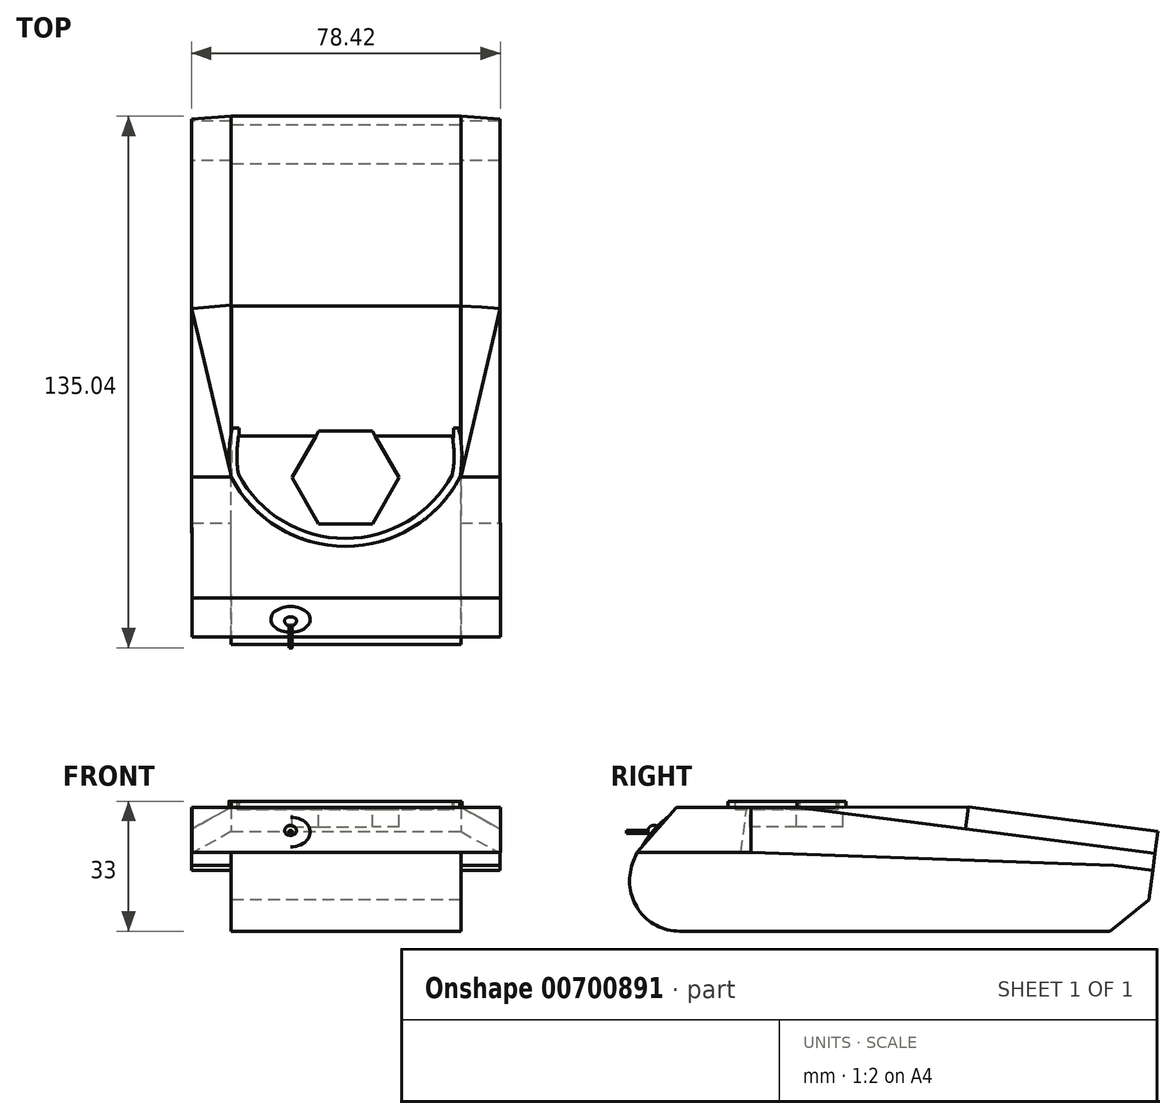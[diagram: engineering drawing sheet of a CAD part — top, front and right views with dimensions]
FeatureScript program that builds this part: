
annotation { "Feature Type Name" : "Feature", "Feature Type Description" : "" }
export const myFeature = defineFeature(function(context is Context, id is Id, definition is map)
    precondition{}
    {
        {
            var Q0;
            Q0=qCreatedBy(makeId("Top.planeOp"),FACE);
            var sketch = newSketch(context, id + "F0", { "sketchPlane" : qUnion([Q0])});
            skLineSegment(sketch, "E0.bottom", {"start": v(33.12, -52.33) * mm, "end": v(-25.22, -52.33) * mm});
            skLineSegment(sketch, "E0.top", {"start": v(33.12, 75.36) * mm, "end": v(-25.22, 75.36) * mm});
            skLineSegment(sketch, "E0.left", {"start": v(33.12, -52.33) * mm, "end": v(33.12, 75.36) * mm});
            skLineSegment(sketch, "E0.right", {"start": v(-25.22, -52.33) * mm, "end": v(-25.22, 75.36) * mm});
            skSolve(sketch);
        }
        {
            var Q0;
            Q0 = qSketchRegion(id + "F0", true);
            extrude(context, id + "F1", {"entities" : qUnion([Q0]), "depth" : 20 * mm, "offsetDistance" : 25 * mm});
        }
        {
            var Q0;
            Q0=makeQuery(id+"F1.opExtrude","CAP_FACE",FACE,{"disambiguationData":[OSD([sQuery(id+"F0.wireOp",EDGE,"E0.bottom"),sQuery(id+"F0.wireOp",EDGE,"E0.top"),sQuery(id+"F0.wireOp",EDGE,"E0.left"),sQuery(id+"F0.wireOp",EDGE,"E0.right")])],"isStart":false});
            var sketch = newSketch(context, id + "F2", { "sketchPlane" : qUnion([Q0])});
            skLineSegment(sketch, "E1", {"start": v(33.12, -52.33) * mm, "end": v(43.12, -52.33) * mm});
            skLineSegment(sketch, "E2", {"start": v(43.12, -52.33) * mm, "end": v(-25.22, -52.33) * mm});
            skLineSegment(sketch, "E3", {"start": v(-25.22, -52.33) * mm, "end": v(-35.22, -52.33) * mm});
            skLineSegment(sketch, "E4.bottom", {"start": v(43.12, -52.33) * mm, "end": v(-35.22, -52.33) * mm});
            skLineSegment(sketch, "E4.top", {"start": v(43.12, 75.36) * mm, "end": v(-35.22, 75.36) * mm});
            skLineSegment(sketch, "E4.left", {"start": v(43.12, -52.33) * mm, "end": v(43.12, 75.36) * mm});
            skLineSegment(sketch, "E4.right", {"start": v(-35.22, -52.33) * mm, "end": v(-35.22, 75.36) * mm});
            skLineSegment(sketch, "E5", {"start": v(43.12, -52.33) * mm, "end": v(43.12, -44.83) * mm});
            skLineSegment(sketch, "E6", {"start": v(43.12, -34.83) * mm, "end": v(-35.22, -34.83) * mm});
            skLineSegment(sketch, "E7", {"start": v(-35.22, -34.83) * mm, "end": v(-35.22, -44.83) * mm});
            skLineSegment(sketch, "E8", {"start": v(33.12, -34.83) * mm, "end": v(-25.22, -34.83) * mm});
            skLineSegment(sketch, "E9", {"start": v(43.12, -44.83) * mm, "end": v(33.12, -44.83) * mm});
            skLineSegment(sketch, "E10", {"start": v(33.12, -44.83) * mm, "end": v(-25.22, -44.83) * mm});
            skLineSegment(sketch, "E11", {"start": v(-25.22, -44.83) * mm, "end": v(-35.22, -44.83) * mm});
            skLineSegment(sketch, "E12", {"start": v(0, -34.83) * mm, "end": v(0, -52.33) * mm});
            skLineSegment(sketch, "E13", {"start": v(0, -52.33) * mm, "end": v(0, -34.83) * mm});
            skLineSegment(sketch, "E14", {"start": v(0, -34.83) * mm, "end": v(0, 75.36) * mm});
            skLineSegment(sketch, "E15.top", {"start": v(33.12, -15.83) * mm, "end": v(-25.22, -15.83) * mm});
            skLineSegment(sketch, "E15.left", {"start": v(33.12, -34.83) * mm, "end": v(33.12, -15.83) * mm});
            skLineSegment(sketch, "E15.right", {"start": v(-25.22, -34.83) * mm, "end": v(-25.22, -15.83) * mm});
            skLineSegment(sketch, "E16", {"start": v(33.12, -15.83) * mm, "end": v(43.12, -15.83) * mm});
            skLineSegment(sketch, "E17", {"start": v(43.12, -15.83) * mm, "end": v(-25.22, -15.83) * mm});
            skLineSegment(sketch, "E18", {"start": v(-25.22, -15.83) * mm, "end": v(-35.22, -15.83) * mm});
            skSolve(sketch);
        }
        {
            var Q0;
            {var subQ0=sQuery(id+"F2.wireOp",EDGE,"E15.left");Q0=makeQuery(id+"F2.imprint","IMPRINT",FACE,{"disambiguationData":[TD([[makeQuery(id+"F2.imprint","IMPRINT",EDGE,{"derivedFrom":subQ0}),1.0]])]});}
            var Q1;
            {var subQ3=sQuery(id+"F2.wireOp",EDGE,"E15.right");Q1=makeQuery(id+"F2.imprint","IMPRINT",FACE,{"disambiguationData":[TD([[makeQuery(id+"F2.imprint","IMPRINT",EDGE,{"derivedFrom":subQ3}),-1.0]])]});}
            extrude(context, id + "F3", {"entities" : qUnion([Q0, Q1]), "operationType" : NewBodyOperationType.ADD, "depth" : 11.5 * mm, "offsetDistance" : 25 * mm});
        }
        {
            var Q0;
            {var subQ0=sQuery(id+"F2.wireOp",EDGE,"E12");var subQ5=sQuery(id+"F2.wireOp",EDGE,"E10");var subQ7=makeQuery(id+"F2.imprint","INTERSECT",VERTEX,{"derivedFrom":[subQ5,subQ0]});Q0=makeQuery(id+"F2.imprint","IMPRINT",FACE,{"disambiguationData":[TD([[makeQuery(id+"F2.imprint","IMPRINT",EDGE,{"disambiguationData":[TD([[subQ7,-1.0]])],"derivedFrom":subQ5}),-1.0]])]});}
            var Q1;
            {var subQ3=sQuery(id+"F2.wireOp",EDGE,"E12");var subQ5=sQuery(id+"F2.wireOp",EDGE,"E10");var subQ7=makeQuery(id+"F2.imprint","INTERSECT",VERTEX,{"derivedFrom":[subQ5,subQ3]});Q1=makeQuery(id+"F2.imprint","IMPRINT",FACE,{"disambiguationData":[TD([[makeQuery(id+"F2.imprint","IMPRINT",EDGE,{"disambiguationData":[TD([[subQ7,1.0]])],"derivedFrom":subQ5}),-1.0]])]});}
            var Q2;
            {var subQ0=sQuery(id+"F2.wireOp",EDGE,"E9");Q2=makeQuery(id+"F2.imprint","IMPRINT",FACE,{"disambiguationData":[TD([[makeQuery(id+"F2.imprint","IMPRINT",EDGE,{"derivedFrom":subQ0}),-1.0]])]});}
            var Q3;
            {var subQ0=sQuery(id+"F2.wireOp",EDGE,"E11");Q3=makeQuery(id+"F2.imprint","IMPRINT",FACE,{"disambiguationData":[TD([[makeQuery(id+"F2.imprint","IMPRINT",EDGE,{"derivedFrom":subQ0}),-1.0]])]});}
            var Q4;
            {var subQ4=sQuery(id+"F2.wireOp",EDGE,"E15.right");Q4=makeQuery(id+"F2.imprint","IMPRINT",FACE,{"disambiguationData":[TD([[makeQuery(id+"F2.imprint","IMPRINT",EDGE,{"derivedFrom":subQ4}),1.0]])]});}
            var Q5;
            {var subQ4=sQuery(id+"F2.wireOp",EDGE,"E15.left");Q5=makeQuery(id+"F2.imprint","IMPRINT",FACE,{"disambiguationData":[TD([[makeQuery(id+"F2.imprint","IMPRINT",EDGE,{"derivedFrom":subQ4}),-1.0]])]});}
            extrude(context, id + "F4", {"entities" : qUnion([Q0, Q1, Q2, Q3, Q4, Q5]), "operationType" : NewBodyOperationType.ADD, "depth" : 11.5 * mm, "offsetDistance" : 25 * mm});
        }
        {
            var Q0;
            Q0=makeQuery(id+"F4.opExtrude","CAP_EDGE",EDGE,{"disambiguationData":[OSD([sQuery(id+"F2.wireOp",EDGE,"E9"),sQuery(id+"F2.wireOp",EDGE,"E10"),sQuery(id+"F2.wireOp",EDGE,"E11")])],"isStart":false});
            chamfer(context, id + "F5", {"entities" : qUnion([Q0]), "chamferType" : ChamferType.TWO_OFFSETS, "width1" : 11.5 * mm, "oppositeDirection" : false, "width2" : 10 * mm, "tangentPropagation" : true});
        }
        {
            var Q0;
            Q0=makeQuery(id+"F4.opExtrude","SWEPT_FACE",FACE,{"disambiguationData":[OSD([sQuery(id+"F2.wireOp",EDGE,"E4.right")])]});
            var sketch = newSketch(context, id + "F6", { "sketchPlane" : qUnion([Q0])});
            skLineSegment(sketch, "E19", {"start": v(15.83, 31.5) * mm, "end": v(-75.36, 20) * mm});
            skSolve(sketch);
        }
        {
            var Q0;
            {var subQ0=sQuery(id+"F2.wireOp",EDGE,"E15.right");var subQ1=sQuery(id+"F2.wireOp",EDGE,"E15.left");var subQ2=sQuery(id+"F2.wireOp",EDGE,"E6");Q0=makeQuery(id+"F4.boolean.opBoolean","MERGE",FACE,{"derivedFrom":[makeQuery(id+"F3.opExtrude","CAP_FACE",FACE,{"disambiguationData":[OSD([subQ2,sQuery(id+"F2.wireOp",EDGE,"E15.top"),subQ1,subQ0])],"isStart":false}),makeQuery(id+"F4.opExtrude","CAP_FACE",FACE,{"disambiguationData":[OSD([sQuery(id+"F2.wireOp",EDGE,"E4.left"),sQuery(id+"F2.wireOp",EDGE,"E4.right"),subQ2,sQuery(id+"F2.wireOp",EDGE,"E9"),sQuery(id+"F2.wireOp",EDGE,"E10"),sQuery(id+"F2.wireOp",EDGE,"E11"),subQ1,subQ0,sQuery(id+"F2.wireOp",EDGE,"E16"),sQuery(id+"F2.wireOp",EDGE,"E18")])],"isStart":false})]});}
            var sketch = newSketch(context, id + "F7", { "sketchPlane" : qUnion([Q0])});
            skLineSegment(sketch, "E20.bottom", {"start": v(-35.22, -15.83) * mm, "end": v(43.12, -15.83) * mm});
            skLineSegment(sketch, "E20.top", {"start": v(-35.22, 75) * mm, "end": v(43.12, 75) * mm});
            skLineSegment(sketch, "E20.left", {"start": v(-35.22, -15.83) * mm, "end": v(-35.22, 75) * mm});
            skLineSegment(sketch, "E20.right", {"start": v(43.12, -15.83) * mm, "end": v(43.12, 75) * mm});
            skSolve(sketch);
        }
        {
            var Q0;
            Q0=sQuery(id+"F7.wireOp",EDGE,"E20.bottom");
            cPlane(context, id + "F8", {"entities" : qUnion([Q0]), "cplaneType" : CPlaneType.LINE_ANGLE, "offset" : 11.5 * mm, "angle" : 97.33 * degree, "oppositeDirection" : true, "width" : 150 * mm, "height" : 150 * mm});
        }
        {
            var Q0;
            Q0=qCreatedBy(id+"F8.planeOp",FACE);
            var sketch = newSketch(context, id + "F9", { "sketchPlane" : qUnion([Q0])});
            skLineSegment(sketch, "E21.bottom", {"start": v(-35.3, 20.78) * mm, "end": v(43.04, 20.78) * mm});
            skLineSegment(sketch, "E21.top", {"start": v(-35.3, -73.57) * mm, "end": v(43.04, -73.57) * mm});
            skLineSegment(sketch, "E21.left", {"start": v(-35.3, 20.78) * mm, "end": v(-35.3, -73.57) * mm});
            skLineSegment(sketch, "E21.right", {"start": v(43.04, 20.78) * mm, "end": v(43.04, -73.57) * mm});
            skSolve(sketch);
        }
        {
            var Q0;
            Q0 = qSketchRegion(id + "F9", true);
            extrude(context, id + "F10", {"entities" : qUnion([Q0]), "operationType" : NewBodyOperationType.ADD, "depth" : 11.7 * mm, "offsetDistance" : 25 * mm});
        }
        {
            var Q0;
            {var subQ0=sQuery(id+"F9.wireOp",EDGE,"E21.top");Q0=makeQuery(id+"F10.boolean.opBoolean","SPLIT",EDGE,{"disambiguationData":[TD([makeQuery(id+"F1.opExtrude","SWEPT_FACE",FACE,{"disambiguationData":[OSD([sQuery(id+"F0.wireOp",EDGE,"E0.left")])]})])],"derivedFrom":makeQuery(id+"F10.opExtrude","CAP_EDGE",EDGE,{"disambiguationData":[OSD([subQ0])],"isStart":false})});}
            var Q1;
            {var subQ1=sQuery(id+"F9.wireOp",EDGE,"E21.top");Q1=makeQuery(id+"F10.boolean.opBoolean","SPLIT",EDGE,{"disambiguationData":[TD([makeQuery(id+"F1.opExtrude","SWEPT_FACE",FACE,{"disambiguationData":[OSD([sQuery(id+"F0.wireOp",EDGE,"E0.right")])]})])],"derivedFrom":makeQuery(id+"F10.opExtrude","CAP_EDGE",EDGE,{"disambiguationData":[OSD([subQ1])],"isStart":false})});}
            chamfer(context, id + "F11", {"entities" : qUnion([Q0, Q1]), "chamferType" : ChamferType.TWO_OFFSETS, "width1" : 8.75 * mm, "oppositeDirection" : true, "width2" : 95 * mm, "tangentPropagation" : true});
        }
        {
            var Q0;
            Q0=makeQuery(id+"F10.opExtrude","CAP_FACE",FACE,{"disambiguationData":[OSD([sQuery(id+"F9.wireOp",EDGE,"E21.bottom"),sQuery(id+"F9.wireOp",EDGE,"E21.top"),sQuery(id+"F9.wireOp",EDGE,"E21.left"),sQuery(id+"F9.wireOp",EDGE,"E21.right")])],"isStart":true});
            extrude(context, id + "F12", {"entities" : qUnion([Q0]), "operationType" : NewBodyOperationType.ADD, "depth" : 1.5 * mm, "offsetDistance" : 25 * mm});
        }
        {
            var Q0;
            {var subQ0=sQuery(id+"F9.wireOp",EDGE,"E21.top");Q0=makeQuery(id+"F12.boolean.opBoolean","MERGE",FACE,{"derivedFrom":[makeQuery(id+"F10.opExtrude","SWEPT_FACE",FACE,{"disambiguationData":[OSD([subQ0])]}),makeQuery(id+"F12.opExtrude","SWEPT_FACE",FACE,{"disambiguationData":[OSD([subQ0])]})]});}
            var sketch = newSketch(context, id + "F13", { "sketchPlane" : qUnion([Q0])});
            skLineSegment(sketch, "E22.bottom", {"start": v(-43.04, 26.27) * mm, "end": v(35.3, 26.27) * mm});
            skLineSegment(sketch, "E22.top", {"start": v(-43.04, 30.72) * mm, "end": v(35.3, 30.72) * mm});
            skLineSegment(sketch, "E22.left", {"start": v(-43.04, 26.27) * mm, "end": v(-43.04, 30.72) * mm});
            skLineSegment(sketch, "E22.right", {"start": v(35.3, 26.27) * mm, "end": v(35.3, 30.72) * mm});
            skLineSegment(sketch, "E23", {"start": v(-33.12, 26.27) * mm, "end": v(25.22, 26.27) * mm});
            skLineSegment(sketch, "E24", {"start": v(25.22, 26.27) * mm, "end": v(-3.95, 26.27) * mm});
            skLineSegment(sketch, "E25", {"start": v(10.63, 26.27) * mm, "end": v(-3.95, 26.27) * mm});
            skLineSegment(sketch, "E26", {"start": v(-3.95, 26.27) * mm, "end": v(-33.12, 26.27) * mm});
            skLineSegment(sketch, "E27", {"start": v(-18.54, 26.27) * mm, "end": v(-3.95, 26.27) * mm});
            skLineSegment(sketch, "E28.bottom", {"start": v(-18.54, 26.27) * mm, "end": v(10.63, 26.27) * mm});
            skLineSegment(sketch, "E28.top", {"start": v(-18.54, 36.28) * mm, "end": v(10.63, 36.28) * mm});
            skLineSegment(sketch, "E28.left", {"start": v(-18.54, 26.27) * mm, "end": v(-18.54, 36.28) * mm});
            skLineSegment(sketch, "E28.right", {"start": v(10.63, 26.27) * mm, "end": v(10.63, 36.28) * mm});
            skLineSegment(sketch, "E29.bottom", {"start": v(25.22, 26.27) * mm, "end": v(10.63, 26.27) * mm});
            skLineSegment(sketch, "E29.top", {"start": v(25.22, 36.28) * mm, "end": v(10.63, 36.28) * mm});
            skLineSegment(sketch, "E29.left", {"start": v(25.22, 26.27) * mm, "end": v(25.22, 36.28) * mm});
            skLineSegment(sketch, "E30.bottom", {"start": v(-18.54, 26.27) * mm, "end": v(-33.12, 26.27) * mm});
            skLineSegment(sketch, "E30.top", {"start": v(-18.54, 36.28) * mm, "end": v(-33.12, 36.28) * mm});
            skLineSegment(sketch, "E30.right", {"start": v(-33.12, 26.27) * mm, "end": v(-33.12, 36.28) * mm});
            skLineSegment(sketch, "E31", {"start": v(25.22, 36.28) * mm, "end": v(35.3, 30.72) * mm});
            skLineSegment(sketch, "E32", {"start": v(-33.12, 36.28) * mm, "end": v(-43.04, 30.72) * mm});
            skSolve(sketch);
        }
        {
            var Q0;
            Q0 = qSketchRegion(id + "F13", true);
            extrude(context, id + "F14", {"entities" : qUnion([Q0]), "operationType" : NewBodyOperationType.ADD, "oppositeDirection" : true, "depth" : 38.55 * mm, "offsetDistance" : 25 * mm});
        }
        {
            var Q0;
            Q0=makeQuery(id+"F7.imprint","IMPRINT",FACE,{"disambiguationData":[TD([[makeQuery(id+"F7.imprint","IMPRINT",EDGE,{"derivedFrom":sQuery(id+"F7.wireOp",EDGE,"E20.bottom")}),-1.0]])]});
            var sketch = newSketch(context, id + "F15", { "sketchPlane" : qUnion([Q0])});
            skLineSegment(sketch, "E33.bottom", {"start": v(-25.2, 39.38) * mm, "end": v(33.1, 39.38) * mm});
            skLineSegment(sketch, "E33.top", {"start": v(-25.2, -14.15) * mm, "end": v(33.1, -14.15) * mm});
            skLineSegment(sketch, "E33.left", {"start": v(-25.2, 39.38) * mm, "end": v(-25.2, -14.15) * mm});
            skLineSegment(sketch, "E33.right", {"start": v(33.1, 39.38) * mm, "end": v(33.1, -14.15) * mm});
            skSolve(sketch);
        }
        {
            var Q0;
            Q0 = qSketchRegion(id + "F15", true);
            extrude(context, id + "F16", {"entities" : qUnion([Q0]), "operationType" : NewBodyOperationType.ADD, "oppositeDirection" : true, "depth" : 11.5 * mm, "offsetDistance" : 25 * mm});
        }
        {
            var Q0;
            Q0=makeQuery(id+"F14.opExtrude","CAP_VERTEX",VERTEX,{"disambiguationData":[OSD([sQuery(id+"F13.wireOp",EDGE,"E22.top"),sQuery(id+"F13.wireOp",EDGE,"E22.right"),sQuery(id+"F13.wireOp",EDGE,"E31")])],"isStart":false});
            var Q1;
            {var subQ0=sQuery(id+"F15.wireOp",EDGE,"E33.left");Q1=makeQuery(id+"F16.boolean.opBoolean","INTERSECT",VERTEX,{"derivedFrom":[makeQuery(id+"F12.opExtrude","CAP_FACE",FACE,{"disambiguationData":[OSD([sQuery(id+"F9.wireOp",EDGE,"E21.bottom"),sQuery(id+"F9.wireOp",EDGE,"E21.top"),sQuery(id+"F9.wireOp",EDGE,"E21.left"),sQuery(id+"F9.wireOp",EDGE,"E21.right")])],"isStart":false}),makeQuery(id+"F16.opExtrude","CAP_FACE",FACE,{"disambiguationData":[OSD([sQuery(id+"F15.wireOp",EDGE,"E33.bottom"),sQuery(id+"F15.wireOp",EDGE,"E33.top"),subQ0,sQuery(id+"F15.wireOp",EDGE,"E33.right")])],"isStart":true}),makeQuery(id+"F16.opExtrude","SWEPT_FACE",FACE,{"disambiguationData":[OSD([subQ0])]})]});}
            var Q2;
            Q2=makeQuery(id+"F14.opExtrude","CAP_VERTEX",VERTEX,{"disambiguationData":[OSD([sQuery(id+"F13.wireOp",EDGE,"E29.top"),sQuery(id+"F13.wireOp",EDGE,"E29.left"),sQuery(id+"F13.wireOp",EDGE,"E31")])],"isStart":false});
            cPlane(context, id + "F17", {"entities" : qUnion([Q0, Q1, Q2]), "cplaneType" : CPlaneType.THREE_POINT, "offset" : 25 * mm, "width" : 150 * mm, "height" : 150 * mm});
        }
        {
            var Q0;
            Q0=qCreatedBy(id+"F17.planeOp",FACE);
            var sketch = newSketch(context, id + "F18", { "sketchPlane" : qUnion([Q0])});
            skLineSegment(sketch, "E34", {"start": v(-7.04, -39.51) * mm, "end": v(-7.04, 4.07) * mm});
            skLineSegment(sketch, "E35", {"start": v(-7.04, 4.07) * mm, "end": v(-18.5, -38.64) * mm});
            skLineSegment(sketch, "E36", {"start": v(-18.5, -38.64) * mm, "end": v(-7.04, -39.51) * mm});
            skSolve(sketch);
        }
        {
            var Q0;
            Q0 = qSketchRegion(id + "F18", true);
            extrude(context, id + "F19", {"entities" : qUnion([Q0]), "operationType" : NewBodyOperationType.ADD, "depth" : 5.4 * mm, "offsetDistance" : 25 * mm});
        }
        {
            var Q0;
            {var subQ0=sQuery(id+"F15.wireOp",EDGE,"E33.right");Q0=makeQuery(id+"F16.boolean.opBoolean","INTERSECT",VERTEX,{"derivedFrom":[makeQuery(id+"F12.opExtrude","CAP_FACE",FACE,{"disambiguationData":[OSD([sQuery(id+"F9.wireOp",EDGE,"E21.bottom"),sQuery(id+"F9.wireOp",EDGE,"E21.top"),sQuery(id+"F9.wireOp",EDGE,"E21.left"),sQuery(id+"F9.wireOp",EDGE,"E21.right")])],"isStart":false}),makeQuery(id+"F16.opExtrude","CAP_FACE",FACE,{"disambiguationData":[OSD([sQuery(id+"F15.wireOp",EDGE,"E33.bottom"),sQuery(id+"F15.wireOp",EDGE,"E33.top"),sQuery(id+"F15.wireOp",EDGE,"E33.left"),subQ0])],"isStart":true}),makeQuery(id+"F16.opExtrude","SWEPT_FACE",FACE,{"disambiguationData":[OSD([subQ0])]})]});}
            var Q1;
            Q1=makeQuery(id+"F14.opExtrude","CAP_VERTEX",VERTEX,{"disambiguationData":[OSD([sQuery(id+"F13.wireOp",EDGE,"E22.top"),sQuery(id+"F13.wireOp",EDGE,"E22.left"),sQuery(id+"F13.wireOp",EDGE,"E32")])],"isStart":false});
            var Q2;
            Q2=makeQuery(id+"F14.opExtrude","CAP_VERTEX",VERTEX,{"disambiguationData":[OSD([sQuery(id+"F13.wireOp",EDGE,"E30.top"),sQuery(id+"F13.wireOp",EDGE,"E30.right"),sQuery(id+"F13.wireOp",EDGE,"E32")])],"isStart":false});
            cPlane(context, id + "F20", {"entities" : qUnion([Q0, Q1, Q2]), "cplaneType" : CPlaneType.THREE_POINT, "offset" : 25 * mm, "width" : 150 * mm, "height" : 150 * mm});
        }
        {
            var Q0;
            Q0=qCreatedBy(id+"F20.planeOp",FACE);
            var sketch = newSketch(context, id + "F21", { "sketchPlane" : qUnion([Q0])});
            skLineSegment(sketch, "E37", {"start": v(13.61, 4.04) * mm, "end": v(13.61, -39.38) * mm});
            skLineSegment(sketch, "E38", {"start": v(13.61, -39.38) * mm, "end": v(25, -38.67) * mm});
            skLineSegment(sketch, "E39", {"start": v(25, -38.67) * mm, "end": v(13.61, 4.04) * mm});
            skSolve(sketch);
        }
        {
            var Q0;
            Q0 = qSketchRegion(id + "F21", true);
            extrude(context, id + "F22", {"entities" : qUnion([Q0]), "operationType" : NewBodyOperationType.ADD, "depth" : 6.9 * mm, "offsetDistance" : 25 * mm});
        }
        {
            var Q0;
            {var subQ0=sQuery(id+"F9.wireOp",EDGE,"E21.left");Q0=makeQuery(id+"F12.boolean.opBoolean","MERGE",FACE,{"derivedFrom":[makeQuery(id+"F10.opExtrude","SWEPT_FACE",FACE,{"disambiguationData":[OSD([subQ0])]}),makeQuery(id+"F12.opExtrude","SWEPT_FACE",FACE,{"disambiguationData":[OSD([subQ0])]})]});}
            var sketch = newSketch(context, id + "F23", { "sketchPlane" : qUnion([Q0])});
            skLineSegment(sketch, "E40", {"start": v(16.9, 31.5) * mm, "end": v(4.08, 31.5) * mm});
            skLineSegment(sketch, "E41", {"start": v(4.08, 31.5) * mm, "end": v(16.69, 33.12) * mm});
            skLineSegment(sketch, "E42", {"start": v(16.69, 33.12) * mm, "end": v(16.9, 31.5) * mm});
            skSolve(sketch);
        }
        {
            var Q0;
            Q0 = qSketchRegion(id + "F23", true);
            extrude(context, id + "F24", {"entities" : qUnion([Q0]), "operationType" : NewBodyOperationType.REMOVE, "oppositeDirection" : true, "depth" : 83 * mm, "offsetDistance" : 25 * mm});
        }
        {
            var Q0;
            Q0=makeQuery(id+"F7.imprint","IMPRINT",FACE,{"disambiguationData":[TD([[makeQuery(id+"F7.imprint","IMPRINT",EDGE,{"derivedFrom":sQuery(id+"F7.wireOp",EDGE,"E20.bottom")}),-1.0]])]});
            var sketch = newSketch(context, id + "F25", { "sketchPlane" : qUnion([Q0])});
            skArc(sketch, "E43", {"start": v(-25.31, -4.11) * mm, "mid": v(3.75, -21.74) * mm, "end": v(32.86, -4.19) * mm});
            skArc(sketch, "E44", {"start": v(32.86, -4.19) * mm, "mid": v(33.36, 2.08) * mm, "end": v(32.52, 8.32) * mm});
            skLineSegment(sketch, "E45", {"start": v(32.52, 8.32) * mm, "end": v(-24.96, 8.32) * mm});
            skArc(sketch, "E46.trimOffspring", {"start": v(-24.96, 8.32) * mm, "mid": v(-25.8, 2.12) * mm, "end": v(-25.31, -4.11) * mm});
            skSolve(sketch);
        }
        {
            var Q0;
            {var subQ1=sQuery(id+"F0.wireOp",EDGE,"E0.right");var subQ3=sQuery(id+"F0.wireOp",EDGE,"E0.bottom");var subQ4=sQuery(id+"F2.wireOp",EDGE,"E15.right");Q0=makeQuery(id+"F10.boolean.opBoolean","SPLIT",FACE,{"disambiguationData":[TD([makeQuery(id+"F1.opExtrude","SWEPT_FACE",FACE,{"disambiguationData":[OSD([subQ3])]})])],"derivedFrom":makeQuery(id+"F3.boolean.opBoolean","MERGE",FACE,{"derivedFrom":[makeQuery(id+"F1.opExtrude","SWEPT_FACE",FACE,{"disambiguationData":[OSD([subQ1])]}),makeQuery(id+"F3.opExtrude","SWEPT_FACE",FACE,{"disambiguationData":[OSD([subQ4])]})]})});}
            var sketch = newSketch(context, id + "F26", { "sketchPlane" : qUnion([Q0])});
            skLineSegment(sketch, "E47", {"start": v(44.83, 20) * mm, "end": v(52.33, 0) * mm});
            skLineSegment(sketch, "E48", {"start": v(52.33, 0) * mm, "end": v(52.33, 20) * mm});
            skLineSegment(sketch, "E49", {"start": v(44.83, 20) * mm, "end": v(52.33, 20) * mm});
            skSolve(sketch);
        }
        {
            var Q0;
            Q0 = qSketchRegion(id + "F26", true);
            extrude(context, id + "F27", {"entities" : qUnion([Q0]), "operationType" : NewBodyOperationType.REMOVE, "oppositeDirection" : true, "depth" : 58.7 * mm, "offsetDistance" : 25 * mm});
        }
        {
            var Q0;
            Q0=makeQuery(id+"F27.boolean.opBoolean","MERGE",EDGE,{"derivedFrom":[makeQuery(id+"F1.opExtrude","CAP_EDGE",EDGE,{"disambiguationData":[OSD([sQuery(id+"F0.wireOp",EDGE,"E0.bottom")])],"isStart":true}),makeQuery(id+"F27.opExtrude","SWEPT_EDGE",EDGE,{"disambiguationData":[OSD([sQuery(id+"F0.wireOp",EDGE,"E0.right"),sQuery(id+"F26.wireOp",EDGE,"E47"),sQuery(id+"F26.wireOp",EDGE,"E48")])]})]});
            fillet(context, id + "F28", {"entities" : qUnion([Q0]), "radius" : 12.7 * mm, "tangentPropagation" : true, "allowEdgeOverflow" : false});
        }
        {
            var Q0;
            Q0=makeQuery(id+"F5.opChamfer","BLEND_FACE",FACE,{"disambiguationData":[OSD([sQuery(id+"F2.wireOp",EDGE,"E9"),sQuery(id+"F2.wireOp",EDGE,"E10"),sQuery(id+"F2.wireOp",EDGE,"E11")])]});
            var sketch = newSketch(context, id + "F29", { "sketchPlane" : qUnion([Q0])});
            skCircle(sketch, "E50", {"center": v(-10.18, -7.44) * mm, "radius": 5 * mm});
            skSolve(sketch);
        }
        {
            var Q0;
            Q0 = qSketchRegion(id + "F29", true);
            extrude(context, id + "F30", {"entities" : qUnion([Q0]), "operationType" : NewBodyOperationType.ADD, "depth" : 0.5 * mm, "offsetDistance" : 25 * mm});
        }
        {
            var Q0;
            Q0=makeQuery(id+"F30.opExtrude","CAP_EDGE",EDGE,{"disambiguationData":[OSD([sQuery(id+"F29.wireOp",EDGE,"E50")])],"isStart":false});
            fillet(context, id + "F31", {"entities" : qUnion([Q0]), "radius" : 24.87 * mm, "tangentPropagation" : true, "allowEdgeOverflow" : false});
        }
        {
            var Q0;
            Q0=makeQuery(id+"F5.opChamfer","BLEND_FACE",FACE,{"disambiguationData":[OSD([sQuery(id+"F2.wireOp",EDGE,"E9"),sQuery(id+"F2.wireOp",EDGE,"E10"),sQuery(id+"F2.wireOp",EDGE,"E11")])]});
            var sketch = newSketch(context, id + "F32", { "sketchPlane" : qUnion([Q0])});
            skCircle(sketch, "E51", {"center": v(-10.18, -7.44) * mm, "radius": 1.52 * mm});
            skSolve(sketch);
        }
        {
            var Q0;
            Q0 = qSketchRegion(id + "F32", true);
            extrude(context, id + "F33", {"entities" : qUnion([Q0]), "operationType" : NewBodyOperationType.ADD, "depth" : 1.8 * mm, "offsetDistance" : 25 * mm});
        }
        {
            var Q0;
            Q0=makeQuery(id+"F33.opExtrude","CAP_FACE",FACE,{"disambiguationData":[OSD([sQuery(id+"F32.wireOp",EDGE,"E51")])],"isStart":false});
            fillet(context, id + "F34", {"entities" : qUnion([Q0]), "radius" : 1.52 * mm, "tangentPropagation" : true, "allowEdgeOverflow" : false});
        }
        {
            var Q0;
            Q0=sQuery(id+"F2.wireOp",EDGE,"E10");
            cPlane(context, id + "F35", {"entities" : qUnion([Q0]), "cplaneType" : CPlaneType.LINE_ANGLE, "offset" : 25 * mm, "angle" : 180 * degree, "width" : 150 * mm, "height" : 150 * mm});
        }
        {
            var Q0;
            Q0=qCreatedBy(id+"F35.planeOp",FACE);
            var sketch = newSketch(context, id + "F36", { "sketchPlane" : qUnion([Q0])});
            skCircle(sketch, "E52", {"center": v(10.16, 25.24) * mm, "radius": 0.42 * mm});
            skSolve(sketch);
        }
        {
            var Q0;
            Q0 = qSketchRegion(id + "F36", true);
            extrude(context, id + "F37", {"entities" : qUnion([Q0]), "operationType" : NewBodyOperationType.ADD, "depth" : 3.5 * mm, "offsetDistance" : 25 * mm, "hasSecondDirection" : true, "secondDirectionOppositeDirection" : true, "secondDirectionDepth" : 2.7 * mm});
        }
        {
            var Q0;
            {var subQ0=sQuery(id+"F9.wireOp",EDGE,"E21.top");Q0=makeQuery(id+"F14.boolean.opBoolean","MERGE",FACE,{"derivedFrom":[makeQuery(id+"F12.boolean.opBoolean","MERGE",FACE,{"derivedFrom":[makeQuery(id+"F10.opExtrude","SWEPT_FACE",FACE,{"disambiguationData":[OSD([subQ0])]}),makeQuery(id+"F12.opExtrude","SWEPT_FACE",FACE,{"disambiguationData":[OSD([subQ0])]})]}),makeQuery(id+"F14.opExtrude","CAP_FACE",FACE,{"disambiguationData":[OSD([sQuery(id+"F13.wireOp",EDGE,"E22.bottom"),sQuery(id+"F13.wireOp",EDGE,"E22.left"),sQuery(id+"F13.wireOp",EDGE,"E22.right"),sQuery(id+"F13.wireOp",EDGE,"E28.bottom"),sQuery(id+"F13.wireOp",EDGE,"E28.top"),sQuery(id+"F13.wireOp",EDGE,"E29.bottom"),sQuery(id+"F13.wireOp",EDGE,"E29.top"),sQuery(id+"F13.wireOp",EDGE,"E30.bottom"),sQuery(id+"F13.wireOp",EDGE,"E30.top"),sQuery(id+"F13.wireOp",EDGE,"E31"),sQuery(id+"F13.wireOp",EDGE,"E32")])],"isStart":true})]});}
            var Q1;
            {var subQ2=sQuery(id+"F0.wireOp",EDGE,"E0.top");Q1=makeQuery(id+"F10.boolean.opBoolean","SPLIT",FACE,{"disambiguationData":[TD([makeQuery(id+"F10.opExtrude","SWEPT_FACE",FACE,{"disambiguationData":[OSD([sQuery(id+"F9.wireOp",EDGE,"E21.top")])]})])],"derivedFrom":makeQuery(id+"F1.opExtrude","SWEPT_FACE",FACE,{"disambiguationData":[OSD([subQ2])]})});}
            extrude(context, id + "F38", {"entities" : qUnion([Q0, Q1]), "operationType" : NewBodyOperationType.ADD, "depth" : 10 * mm, "offsetDistance" : 25 * mm});
        }
        {
            var Q0;
            {var subQ0=sQuery(id+"F9.wireOp",EDGE,"E21.top");var subQ1=sQuery(id+"F2.wireOp",EDGE,"E15.left");var subQ2=sQuery(id+"F0.wireOp",EDGE,"E0.left");var subQ3=sQuery(id+"F0.wireOp",EDGE,"E0.top");var subQ5=sQuery(id+"F0.wireOp",EDGE,"E0.bottom");Q0=makeQuery(id+"F38.boolean.opBoolean","MERGE",FACE,{"derivedFrom":[makeQuery(id+"F10.boolean.opBoolean","SPLIT",FACE,{"disambiguationData":[TD([makeQuery(id+"F1.opExtrude","SWEPT_FACE",FACE,{"disambiguationData":[OSD([subQ5])]})])],"derivedFrom":makeQuery(id+"F3.boolean.opBoolean","MERGE",FACE,{"derivedFrom":[makeQuery(id+"F1.opExtrude","SWEPT_FACE",FACE,{"disambiguationData":[OSD([subQ2])]}),makeQuery(id+"F3.opExtrude","SWEPT_FACE",FACE,{"disambiguationData":[OSD([subQ1])]})]})}),makeQuery(id+"F38.opExtrude","SWEPT_FACE",FACE,{"disambiguationData":[OSD([subQ3,subQ2])]}),makeQuery(id+"F38.opExtrude","SWEPT_FACE",FACE,{"disambiguationData":[OSD([subQ3,subQ2,subQ1,subQ0])]})]});}
            var sketch = newSketch(context, id + "F39", { "sketchPlane" : qUnion([Q0])});
            skLineSegment(sketch, "E53", {"start": v(75.36, 0) * mm, "end": v(85.28, 7.94) * mm});
            skLineSegment(sketch, "E54", {"start": v(85.28, 7.94) * mm, "end": v(85.28, -1.28) * mm});
            skLineSegment(sketch, "E55", {"start": v(85.28, -1.28) * mm, "end": v(75.36, 0) * mm});
            skSolve(sketch);
        }
        {
            var Q0;
            Q0 = qSketchRegion(id + "F39", true);
            extrude(context, id + "F40", {"entities" : qUnion([Q0]), "operationType" : NewBodyOperationType.REMOVE, "oppositeDirection" : true, "depth" : 58.9 * mm, "offsetDistance" : 25 * mm});
        }
        {
            var Q0;
            Q0 = qSketchRegion(id + "F25", true);
            extrude(context, id + "F41", {"entities" : qUnion([Q0]), "operationType" : NewBodyOperationType.ADD, "depth" : 1.5 * mm, "offsetDistance" : 25 * mm});
        }
        {
            var Q0;
            Q0=makeQuery(id+"F41.opExtrude","CAP_FACE",FACE,{"disambiguationData":[OSD([sQuery(id+"F25.wireOp",EDGE,"E43"),sQuery(id+"F25.wireOp",EDGE,"E44"),sQuery(id+"F25.wireOp",EDGE,"E45"),sQuery(id+"F25.wireOp",EDGE,"E46.trimOffspring")])],"isStart":false});
            var sketch = newSketch(context, id + "F42", { "sketchPlane" : qUnion([Q0])});
            skArc(sketch, "E56.0", {"start": v(-23.4, -3.45) * mm, "mid": v(3.75, -19.74) * mm, "end": v(30.95, -3.52) * mm});
            skArc(sketch, "E56.1", {"start": v(-23.34, 6.32) * mm, "mid": v(-23.8, 1.43) * mm, "end": v(-23.4, -3.45) * mm});
            skLineSegment(sketch, "E56.2", {"start": v(30.9, 6.32) * mm, "end": v(-23.34, 6.32) * mm});
            skArc(sketch, "E56.3", {"start": v(30.95, -3.52) * mm, "mid": v(31.37, 1.4) * mm, "end": v(30.9, 6.32) * mm});
            skLineSegment(sketch, "E57", {"start": v(30.9, 6.32) * mm, "end": v(30.9, 8.32) * mm});
            skLineSegment(sketch, "E58", {"start": v(-23.34, 6.32) * mm, "end": v(-23.34, 8.32) * mm});
            skSolve(sketch);
        }
        {
            var Q0;
            Q0=makeQuery(id+"F42.imprint","IMPRINT",FACE,{"disambiguationData":[TD([[makeQuery(id+"F42.imprint","IMPRINT",EDGE,{"derivedFrom":sQuery(id+"F42.wireOp",EDGE,"E56.0")}),1.0]])]});
            extrude(context, id + "F43", {"entities" : qUnion([Q0]), "operationType" : NewBodyOperationType.REMOVE, "oppositeDirection" : true, "depth" : 2 * mm, "offsetDistance" : 25 * mm});
        }
        {
            var Q0;
            {var subQ0=sQuery(id+"F25.wireOp",EDGE,"E44");Q0=makeQuery(id+"F25.imprint","IMPRINT",FACE,{"disambiguationData":[TD([[makeQuery(id+"F25.imprint","IMPRINT",EDGE,{"derivedFrom":subQ0}),1.0]])]});}
            var sketch = newSketch(context, id + "F44", { "sketchPlane" : qUnion([Q0])});
            skPoint(sketch, "E59", {"position": v(3.8, 29.09) * mm});
            skLineSegment(sketch, "E60", {"start": v(3.8, 29.09) * mm, "end": v(3.8, -37.57) * mm});
            skCircle(sketch, "E61.cCircle", {"center": v(3.8, -4.24) * mm, "radius": 11.8 * mm, "construction": true});
            skLineSegment(sketch, "E61.0", {"start": v(10.6, -16.04) * mm, "end": v(-3.02, -16.04) * mm});
            skLineSegment(sketch, "E61.1", {"start": v(-3.02, -16.04) * mm, "end": v(-9.83, -4.24) * mm});
            skLineSegment(sketch, "E61.2", {"start": v(-9.83, -4.24) * mm, "end": v(-3.02, 7.56) * mm});
            skLineSegment(sketch, "E61.3", {"start": v(-3.02, 7.56) * mm, "end": v(10.6, 7.56) * mm});
            skLineSegment(sketch, "E61.4", {"start": v(10.6, 7.56) * mm, "end": v(17.42, -4.24) * mm});
            skLineSegment(sketch, "E61.5", {"start": v(17.42, -4.24) * mm, "end": v(10.6, -16.04) * mm});
            skPoint(sketch, "E61.0.midPoint", {"position": v(3.8, -16.04) * mm});
            skSolve(sketch);
        }
        {
            var Q0;
            Q0 = qSketchRegion(id + "F44", true);
            extrude(context, id + "F45", {"entities" : qUnion([Q0]), "operationType" : NewBodyOperationType.REMOVE, "oppositeDirection" : true, "depth" : 5 * mm, "offsetDistance" : 25 * mm, "hasSecondDirection" : true, "secondDirectionOppositeDirection" : false, "secondDirectionDepth" : 2 * mm});
        }
        {
            var Q0;
            Q0=makeQuery(id+"F41.opExtrude","SWEPT_FACE",FACE,{"disambiguationData":[OSD([sQuery(id+"F25.wireOp",EDGE,"E45")])]});
            var sketch = newSketch(context, id + "F46", { "sketchPlane" : qUnion([Q0])});
            skLineSegment(sketch, "E62.bottom", {"start": v(-31.22, 33) * mm, "end": v(23.26, 33) * mm});
            skLineSegment(sketch, "E62.top", {"start": v(-31.22, 31.5) * mm, "end": v(23.26, 31.5) * mm});
            skLineSegment(sketch, "E62.left", {"start": v(-31.22, 33) * mm, "end": v(-31.22, 31.5) * mm});
            skLineSegment(sketch, "E62.right", {"start": v(23.26, 33) * mm, "end": v(23.26, 31.5) * mm});
            skSolve(sketch);
        }
        {
            var Q0;
            Q0 = qSketchRegion(id + "F46", true);
            extrude(context, id + "F47", {"entities" : qUnion([Q0]), "operationType" : NewBodyOperationType.REMOVE, "oppositeDirection" : true, "depth" : 2.5 * mm, "offsetDistance" : 25 * mm});
        }
    });
